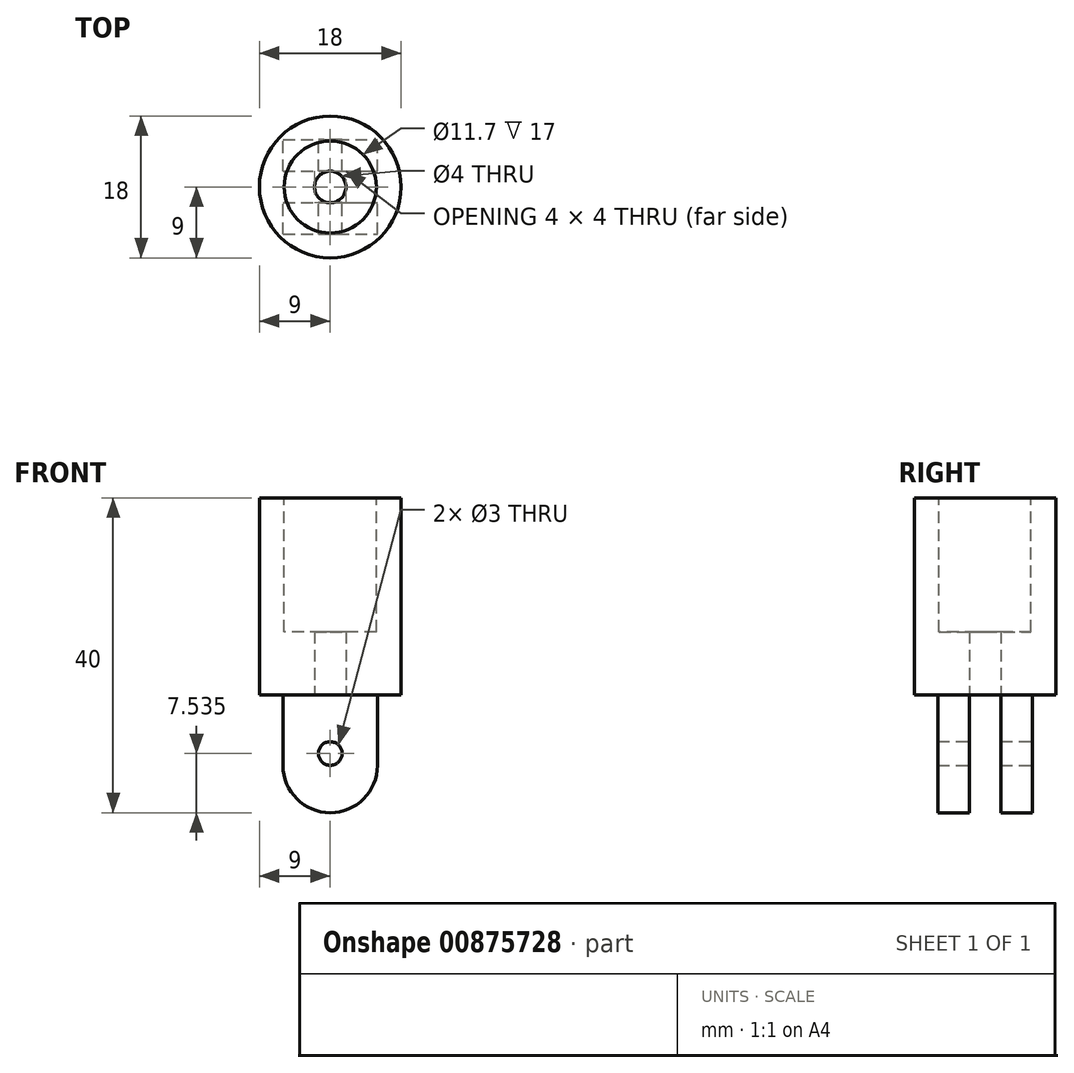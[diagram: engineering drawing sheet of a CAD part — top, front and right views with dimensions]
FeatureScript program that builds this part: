
annotation { "Feature Type Name" : "Feature", "Feature Type Description" : "" }
export const myFeature = defineFeature(function(context is Context, id is Id, definition is map)
    precondition{}
    {
        {
            var Q0;
            Q0=qCreatedBy(makeId("Top.planeOp"),FACE);
            var sketch = newSketch(context, id + "F0", { "sketchPlane" : qUnion([Q0])});
            skCircle(sketch, "E0", {"center": v(0, 0) * mm, "radius": 9 * mm});
            skSolve(sketch);
        }
        {
            var Q0;
            Q0=makeQuery(id+"F0.imprint","IMPRINT",FACE,{"disambiguationData":[TD([[makeQuery(id+"F0.imprint","IMPRINT",EDGE,{"derivedFrom":sQuery(id+"F0.wireOp",EDGE,"E0")}),1.0]])]});
            extrude(context, id + "F1", {"entities" : qUnion([Q0]), "depth" : 25 * mm, "offsetDistance" : 25 * mm});
        }
        {
            var Q0;
            Q0=makeQuery(id+"F1.opExtrude","CAP_FACE",FACE,{"disambiguationData":[OSD([sQuery(id+"F0.wireOp",EDGE,"E0")])],"isStart":true});
            var sketch = newSketch(context, id + "F2", { "sketchPlane" : qUnion([Q0])});
            skLineSegment(sketch, "E1.bottom", {"start": v(-6, 6) * mm, "end": v(6, 6) * mm});
            skLineSegment(sketch, "E1.top", {"start": v(-6, -6) * mm, "end": v(6, -6) * mm});
            skLineSegment(sketch, "E1.left", {"start": v(-6, 6) * mm, "end": v(-6, -6) * mm});
            skLineSegment(sketch, "E1.right", {"start": v(6, 6) * mm, "end": v(6, -6) * mm});
            skPoint(sketch, "E1.middle", {"position": v(0, 0) * mm});
            skLineSegment(sketch, "E2.bottom", {"start": v(-6, -2) * mm, "end": v(6, -2) * mm});
            skLineSegment(sketch, "E2.top", {"start": v(-6, 2) * mm, "end": v(6, 2) * mm});
            skLineSegment(sketch, "E2.left", {"start": v(-6, -2) * mm, "end": v(-6, 2) * mm});
            skLineSegment(sketch, "E2.right", {"start": v(6, -2) * mm, "end": v(6, 2) * mm});
            skSolve(sketch);
        }
        {
            var Q0;
            {var subQ0=sQuery(id+"F2.wireOp",EDGE,"E1.top");Q0=makeQuery(id+"F2.imprint","IMPRINT",FACE,{"disambiguationData":[TD([[makeQuery(id+"F2.imprint","IMPRINT",EDGE,{"derivedFrom":subQ0}),1.0]])]});}
            var Q1;
            {var subQ0=sQuery(id+"F2.wireOp",EDGE,"E1.bottom");Q1=makeQuery(id+"F2.imprint","IMPRINT",FACE,{"disambiguationData":[TD([[makeQuery(id+"F2.imprint","IMPRINT",EDGE,{"derivedFrom":subQ0}),-1.0]])]});}
            extrude(context, id + "F3", {"entities" : qUnion([Q0, Q1]), "operationType" : NewBodyOperationType.ADD, "depth" : 15 * mm, "offsetDistance" : 25 * mm});
        }
        {
            var Q0;
            Q0=makeQuery(id+"F3.opExtrude","SWEPT_FACE",FACE,{"disambiguationData":[OSD([sQuery(id+"F2.wireOp",EDGE,"E1.top")])]});
            var sketch = newSketch(context, id + "F4", { "sketchPlane" : qUnion([Q0])});
            skCircle(sketch, "E3", {"center": v(0, -7.46) * mm, "radius": 1.5 * mm});
            skSolve(sketch);
        }
        {
            var Q0;
            Q0=makeQuery(id+"F4.imprint","IMPRINT",FACE,{"disambiguationData":[TD([[makeQuery(id+"F4.imprint","IMPRINT",EDGE,{"derivedFrom":sQuery(id+"F4.wireOp",EDGE,"E3")}),1.0]])]});
            var Q1;
            Q1=makeQuery(id+"F3.opExtrude","SWEPT_FACE",FACE,{"disambiguationData":[OSD([sQuery(id+"F2.wireOp",EDGE,"E1.bottom")])]});
            extrude(context, id + "F5", {"entities" : qUnion([Q0]), "operationType" : NewBodyOperationType.REMOVE, "endBound" : BoundingType.UP_TO_SURFACE, "oppositeDirection" : true, "depth" : 25 * mm, "endBoundEntityFace" : qUnion([Q1]), "offsetDistance" : 25 * mm});
        }
        {
            var Q0;
            {var subQ0=sQuery(id+"F2.wireOp",EDGE,"E1.left");Q0=makeQuery(id+"F3.opExtrude","CAP_EDGE",EDGE,{"disambiguationData":[OSD([subQ0]),TDD([makeQuery(id+"F2.imprint","IMPRINT",EDGE,{"disambiguationData":[TD([[makeQuery(id+"F2.imprint","INTERSECT",VERTEX,{"derivedFrom":[sQuery(id+"F2.wireOp",EDGE,"E1.top"),subQ0]}),1.0]])],"derivedFrom":subQ0})])],"isStart":false});}
            var Q1;
            {var subQ0=sQuery(id+"F2.wireOp",EDGE,"E1.left");Q1=makeQuery(id+"F3.opExtrude","CAP_EDGE",EDGE,{"disambiguationData":[OSD([subQ0]),TDD([makeQuery(id+"F2.imprint","IMPRINT",EDGE,{"disambiguationData":[TD([[makeQuery(id+"F2.imprint","INTERSECT",VERTEX,{"derivedFrom":[sQuery(id+"F2.wireOp",EDGE,"E1.bottom"),subQ0]}),-1.0]])],"derivedFrom":subQ0})])],"isStart":false});}
            var Q2;
            {var subQ0=sQuery(id+"F2.wireOp",EDGE,"E1.right");Q2=makeQuery(id+"F3.opExtrude","CAP_EDGE",EDGE,{"disambiguationData":[OSD([subQ0]),TDD([makeQuery(id+"F2.imprint","IMPRINT",EDGE,{"disambiguationData":[TD([[makeQuery(id+"F2.imprint","INTERSECT",VERTEX,{"derivedFrom":[sQuery(id+"F2.wireOp",EDGE,"E1.bottom"),subQ0]}),-1.0]])],"derivedFrom":subQ0})])],"isStart":false});}
            var Q3;
            {var subQ0=sQuery(id+"F2.wireOp",EDGE,"E1.right");Q3=makeQuery(id+"F3.opExtrude","CAP_EDGE",EDGE,{"disambiguationData":[OSD([subQ0]),TDD([makeQuery(id+"F2.imprint","IMPRINT",EDGE,{"disambiguationData":[TD([[makeQuery(id+"F2.imprint","INTERSECT",VERTEX,{"derivedFrom":[sQuery(id+"F2.wireOp",EDGE,"E1.top"),subQ0]}),1.0]])],"derivedFrom":subQ0})])],"isStart":false});}
            fillet(context, id + "F6", {"entities" : qUnion([Q0, Q1, Q2, Q3]), "radius" : 6 * mm, "tangentPropagation" : true, "allowEdgeOverflow" : false});
        }
        {
            var Q0;
            Q0=makeQuery(id+"F1.opExtrude","CAP_FACE",FACE,{"disambiguationData":[OSD([sQuery(id+"F0.wireOp",EDGE,"E0")])],"isStart":false});
            var sketch = newSketch(context, id + "F7", { "sketchPlane" : qUnion([Q0])});
            skCircle(sketch, "E4", {"center": v(0, 0) * mm, "radius": 5.85 * mm});
            skSolve(sketch);
        }
        {
            var Q0;
            Q0=makeQuery(id+"F7.imprint","IMPRINT",FACE,{"disambiguationData":[TD([[makeQuery(id+"F7.imprint","IMPRINT",EDGE,{"derivedFrom":sQuery(id+"F7.wireOp",EDGE,"E4")}),1.0]])]});
            extrude(context, id + "F8", {"entities" : qUnion([Q0]), "operationType" : NewBodyOperationType.REMOVE, "oppositeDirection" : true, "depth" : 17 * mm, "offsetDistance" : 25 * mm});
        }
        {
            var Q0;
            Q0=makeQuery(id+"F1.opExtrude","CAP_FACE",FACE,{"disambiguationData":[OSD([sQuery(id+"F0.wireOp",EDGE,"E0")])],"isStart":true});
            var sketch = newSketch(context, id + "F9", { "sketchPlane" : qUnion([Q0])});
            skCircle(sketch, "E5", {"center": v(0, 0) * mm, "radius": 2 * mm});
            skSolve(sketch);
        }
        {
            var Q0;
            {var subQ0=sQuery(id+"F9.wireOp",EDGE,"E5");var subQ1=makeQuery(id+"F9.imprint","INTERSECT",VERTEX,{"derivedFrom":[makeQuery(id+"F3.opExtrude","CAP_EDGE",EDGE,{"disambiguationData":[OSD([sQuery(id+"F2.wireOp",EDGE,"E2.bottom")])],"isStart":true}),subQ0]});Q0=makeQuery(id+"F9.imprint","IMPRINT",FACE,{"disambiguationData":[TD([[makeQuery(id+"F9.imprint","IMPRINT",EDGE,{"disambiguationData":[TD([[subQ1,1.0]])],"derivedFrom":subQ0}),1.0]])]});}
            extrude(context, id + "F10", {"entities" : qUnion([Q0]), "operationType" : NewBodyOperationType.REMOVE, "endBound" : BoundingType.UP_TO_NEXT, "oppositeDirection" : true, "depth" : 25 * mm, "offsetDistance" : 25 * mm});
        }
    });
